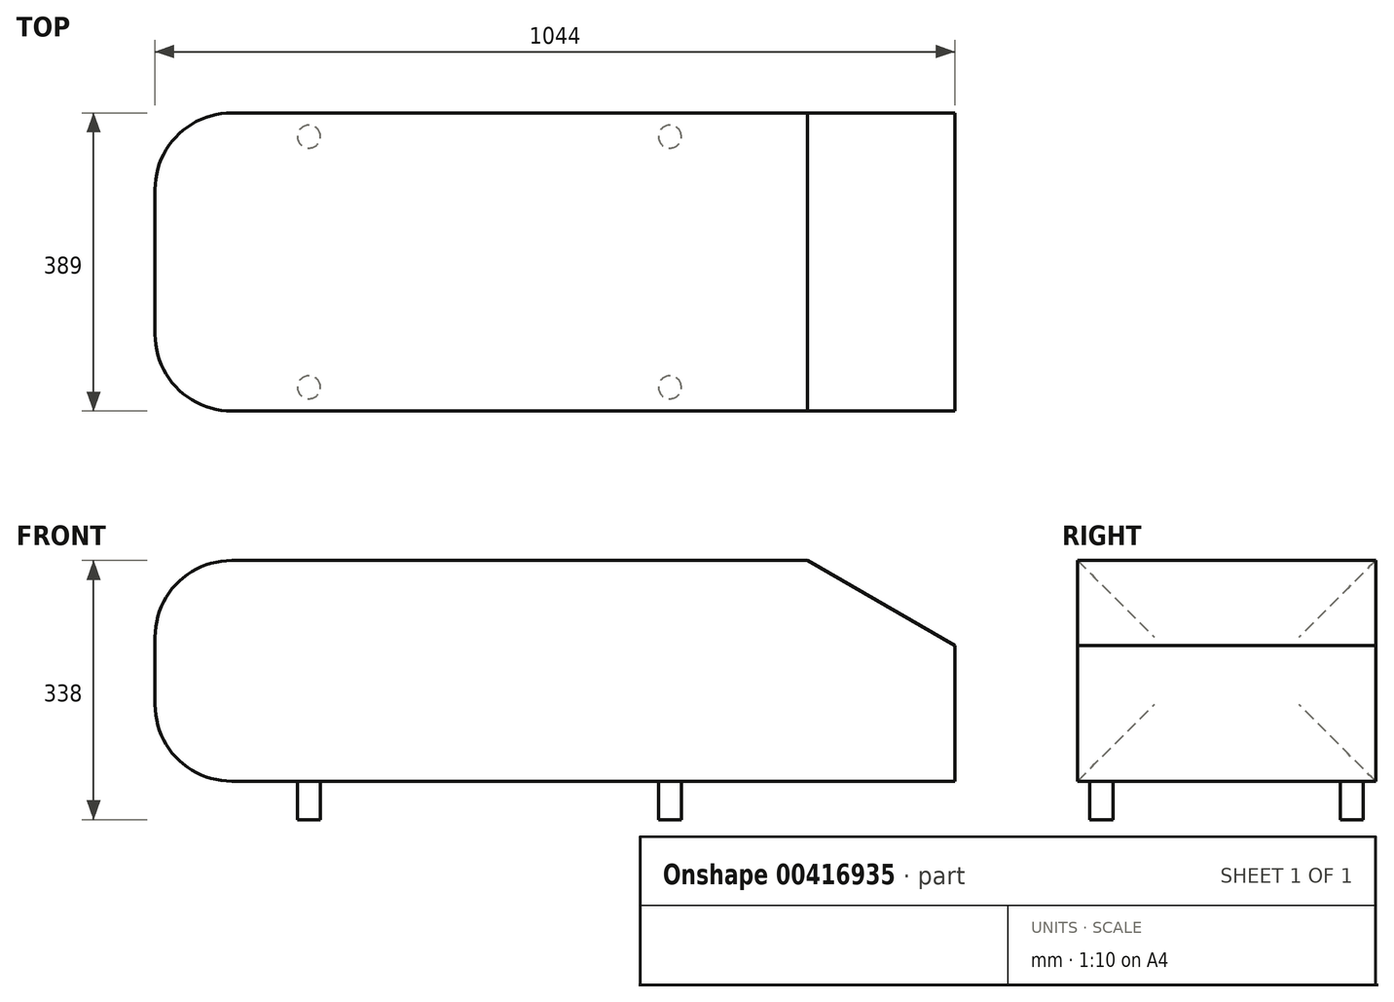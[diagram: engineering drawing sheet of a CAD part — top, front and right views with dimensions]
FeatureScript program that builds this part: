
annotation { "Feature Type Name" : "Feature", "Feature Type Description" : "" }
export const myFeature = defineFeature(function(context is Context, id is Id, definition is map)
    precondition{}
    {
        {
            var Q0;
            Q0=qCreatedBy(makeId("Top.planeOp"),FACE);
            var sketch = newSketch(context, id + "F0", { "sketchPlane" : qUnion([Q0]), "disableImprinting" : false});
            skLineSegment(sketch, "E0.bottom", {"start": v(-522, 194.5) * mm, "end": v(522, 194.5) * mm});
            skLineSegment(sketch, "E0.top", {"start": v(-522, -194.5) * mm, "end": v(522, -194.5) * mm});
            skLineSegment(sketch, "E0.left", {"start": v(-522, 194.5) * mm, "end": v(-522, -194.5) * mm});
            skLineSegment(sketch, "E0.right", {"start": v(522, 194.5) * mm, "end": v(522, -194.5) * mm});
            skSolve(sketch);
        }
        {
            var Q0;
            Q0=makeQuery(id+"F0.imprint","IMPRINT",FACE,{"disambiguationData":[TD([[makeQuery(id+"F0.imprint","IMPRINT",EDGE,{"derivedFrom":sQuery(id+"F0.wireOp",EDGE,"E0.bottom")}),-1.0]])]});
            extrude(context, id + "F1", {"entities" : qUnion([Q0]), "depth" : 288 * mm});
        }
        {
            var Q0;
            Q0=makeQuery(id+"F1.opExtrude","SWEPT_FACE",FACE,{"disambiguationData":[OSD([sQuery(id+"F0.wireOp",EDGE,"E0.top")])]});
            var sketch = newSketch(context, id + "F2", { "sketchPlane" : qUnion([Q0])});
            skLineSegment(sketch, "E1", {"start": v(329.74, 288) * mm, "end": v(522, 177) * mm});
            skLineSegment(sketch, "E2", {"start": v(522, 177) * mm, "end": v(522, 288) * mm});
            skLineSegment(sketch, "E3", {"start": v(522, 288) * mm, "end": v(329.74, 288) * mm});
            skSolve(sketch);
        }
        {
            var Q0;
            Q0 = qSketchRegion(id + "F2", true);
            extrude(context, id + "F3", {"entities" : qUnion([Q0]), "operationType" : NewBodyOperationType.REMOVE, "endBound" : BoundingType.UP_TO_NEXT, "oppositeDirection" : true, "offsetDistance" : 25 * mm, "depth" : 25 * mm});
        }
        {
            var Q0;
            Q0=makeQuery(id+"F1.opExtrude","SWEPT_FACE",FACE,{"disambiguationData":[OSD([sQuery(id+"F0.wireOp",EDGE,"E0.left")])]});
            fillet(context, id + "F4", {"entities" : qUnion([Q0]), "radius" : 100 * mm, "tangentPropagation" : true, "allowEdgeOverflow" : false});
        }
        {
            var Q0;
            Q0=makeQuery(id+"F1.opExtrude","CAP_FACE",FACE,{"disambiguationData":[OSD([sQuery(id+"F0.wireOp",EDGE,"E0.bottom"),sQuery(id+"F0.wireOp",EDGE,"E0.top"),sQuery(id+"F0.wireOp",EDGE,"E0.left"),sQuery(id+"F0.wireOp",EDGE,"E0.right")])],"isStart":true});
            var sketch = newSketch(context, id + "F5", { "sketchPlane" : qUnion([Q0])});
            skCircle(sketch, "E4", {"center": v(150, 163.5) * mm, "radius": 15 * mm});
            skCircle(sketch, "E5", {"center": v(-321, 163.5) * mm, "radius": 15 * mm});
            skLineSegment(sketch, "E6", {"start": v(-422, 0) * mm, "end": v(522, 0) * mm, "construction": true});
            skCircle(sketch, "E7.MirrorC", {"center": v(-321, -163.5) * mm, "radius": 15 * mm});
            skCircle(sketch, "E8.MirrorC", {"center": v(150, -163.5) * mm, "radius": 15 * mm});
            skSolve(sketch);
        }
        {
            var Q0;
            Q0 = qSketchRegion(id + "F5", true);
            extrude(context, id + "F6", {"entities" : qUnion([Q0]), "operationType" : NewBodyOperationType.ADD, "offsetDistance" : 25 * mm, "depth" : 50 * mm});
        }
        {
            var Q0;
            Q0=makeQuery(id+"F1.opExtrude","SWEPT_BODY",BODY,{"disambiguationData":[OSD([sQuery(id+"F0.wireOp",EDGE,"E0.bottom"),sQuery(id+"F0.wireOp",EDGE,"E0.top"),sQuery(id+"F0.wireOp",EDGE,"E0.left"),sQuery(id+"F0.wireOp",EDGE,"E0.right")])]});
            transform(context, id + "F7", {"entities" : qUnion([Q0]), "transformType" : TransformType.TRANSLATION_3D, "dx" : 0 * mm, "dy" : 0 * mm, "dz" : 50 * mm, "makeCopy" : false});
        }
    });
